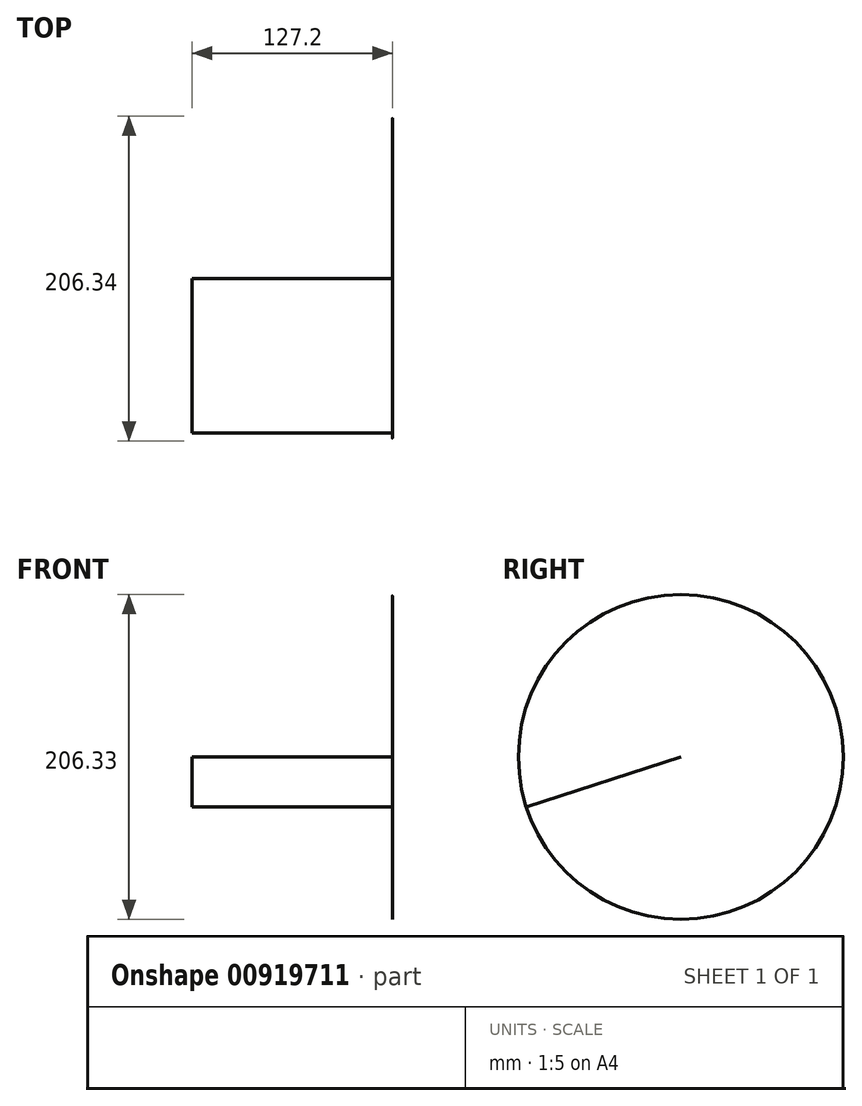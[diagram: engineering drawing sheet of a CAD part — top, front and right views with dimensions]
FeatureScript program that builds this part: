
annotation { "Feature Type Name" : "Feature", "Feature Type Description" : "" }
export const myFeature = defineFeature(function(context is Context, id is Id, definition is map)
    precondition{}
    {
        {
            var Q0;
            Q0=qCreatedBy(makeId("Right.planeOp"),FACE);
            var sketch = newSketch(context, id + "F0", { "sketchPlane" : qUnion([Q0])});
            skLineSegment(sketch, "E0", {"start": v(18.76, 26.17) * mm, "end": v(-217.95, 26.17) * mm});
            skLineSegment(sketch, "E1", {"start": v(-217.95, 26.17) * mm, "end": v(-119.8, 57.96) * mm});
            skSolve(sketch);
        }
        {
            var Q0;
            Q0=sQuery(id+"F0.wireOp",EDGE,"E1");
            extrude(context, id + "F1", {"bodyType" : ToolBodyType.SURFACE, "surfaceEntities" : qUnion([Q0]), "depth" : 127.2 * mm, "offsetDistance" : 25 * mm});
        }
        {
            var Q0;
            Q0=makeQuery(id+"F1.opExtrude","SWEPT_FACE",FACE,{"disambiguationData":[OSD([sQuery(id+"F0.wireOp",EDGE,"E1")])]});
            var sketch = newSketch(context, id + "F2", { "sketchPlane" : qUnion([Q0])});
            skSolve(sketch);
        }
        {
            var Q0;
            Q0=makeQuery(id+"F2.imprint","IMPRINT",FACE,{"disambiguationData":[TD([[makeQuery(id+"F2.imprint","IMPRINT",EDGE,{"derivedFrom":makeQuery(id+"F1.opExtrude","SWEPT_EDGE",EDGE,{"disambiguationData":[OSD([sQuery(id+"F0.wireOp",VERTEX,"E1.start")])]})}),-1.0]])]});
            var Q1;
            Q1=makeQuery(id+"F1.opExtrude","CAP_EDGE",EDGE,{"disambiguationData":[OSD([sQuery(id+"F0.wireOp",EDGE,"E1")])],"isStart":false});
            var Q2;
            Q2=makeQuery(id+"F1.opExtrude","SWEPT_EDGE",EDGE,{"disambiguationData":[OSD([sQuery(id+"F0.wireOp",VERTEX,"E1.end")])]});
            revolve(context, id + "F3", {"bodyType" : ToolBodyType.SURFACE, "surfaceOperationType" : NewSurfaceOperationType.NEW, "entities" : qUnion([Q0]), "surfaceEntities" : qUnion([Q1]), "axis" : qUnion([Q2]), "revolveType" : RevolveType.FULL});
        }
    });
